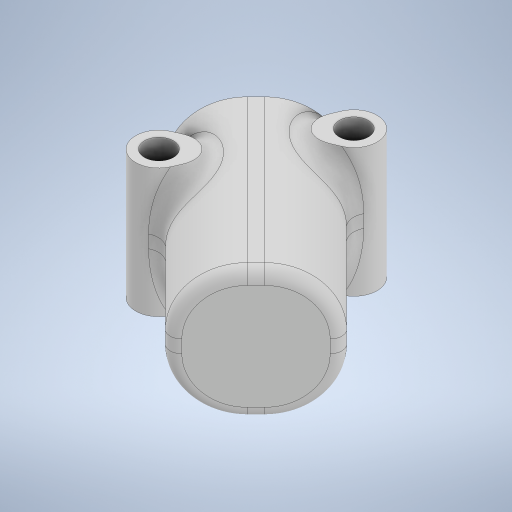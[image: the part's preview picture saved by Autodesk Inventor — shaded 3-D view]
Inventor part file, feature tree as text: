
AUTODESK INVENTOR PART (.ipt)
format: ipt  version: 2023 (Build 270158000, 158)  size: 434,688 bytes
history: native  units: in
note: dims shown in document units (in); Inventor stores cm internally (conversion verified against a paired STEP export)
features: extrude x3, fillet x3, sketch x2, hole x1, projected_geometry x1
ambient origin geometry x8: Origin, YZ Plane, XZ Plane, XY Plane, X Axis, Y Axis, Z Axis, Center Point
bodies: Solid1 (feature_tree)
feature tree (10):
  sketch  "Sketch1"  dims[d0=0.315in d1=0.315in d2=0.0787in]
  extrude  "Extrusion1"  Depth=0.315in
  fillet  "Fillet1"  Radius=0.0787in
  extrude  "Extrusion2"  Depth=0.1181in
  extrude  "Extrusion3"  Depth=0.1181in TaperAngle=0.0deg
  hole  "Hole1"  [1 undecoded]
  fillet  "Fillet2"  Radius=0.874in
  fillet  "Fillet3"  Radius=0.874in
  sketch  "Sketch2"  dims[d3=0.0787in d4=0.0787in d5=0.874in d6=0.0in d7=0.3937in d8=0.874in d9=0.0in d10=0.874in d11=0.0in d12=0.7244in d13=0.2362in d14=0.1575in d15=0.0787in d16=90.0deg d17=1.378in d18=0.0in d19=0.0787in d20=0.1181in]
  projected_geometry  "Projected Loop1"
note: 1 required parameter value undecoded (feature->parameter linkage not recoverable at this tier; creation-order binding heuristic only, values carry confidence <= 0.55)
